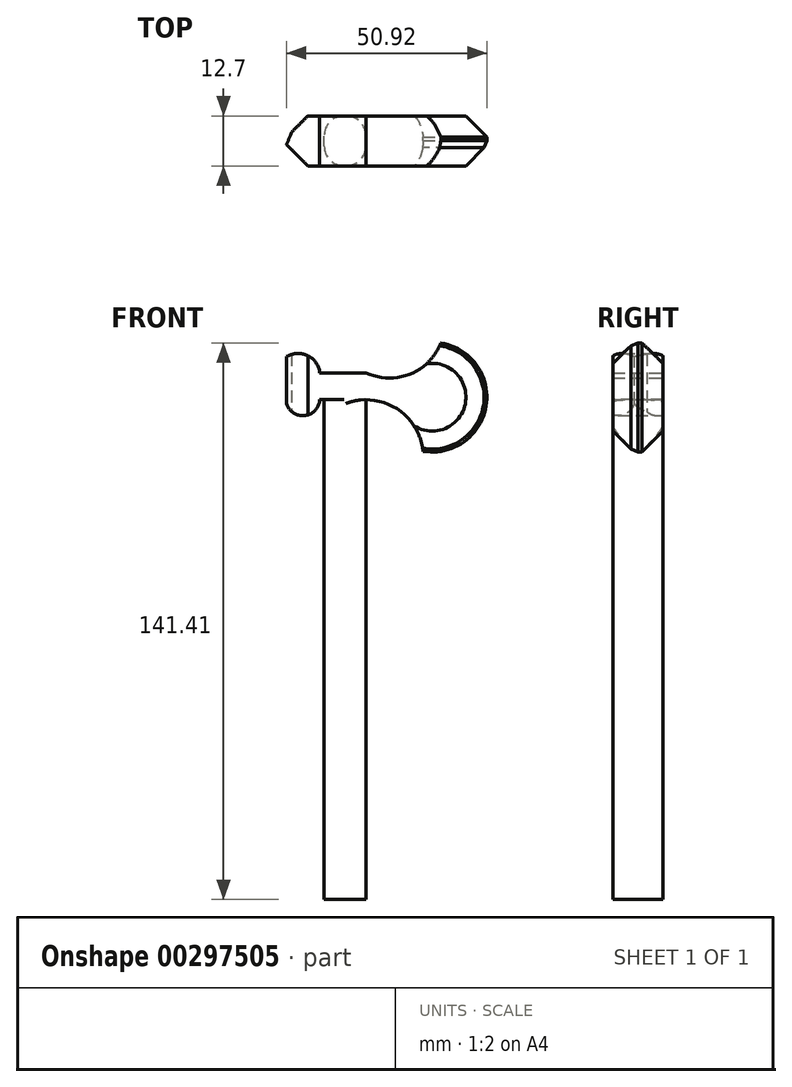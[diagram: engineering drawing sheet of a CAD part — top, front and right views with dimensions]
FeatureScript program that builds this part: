
annotation { "Feature Type Name" : "Feature", "Feature Type Description" : "" }
export const myFeature = defineFeature(function(context is Context, id is Id, definition is map)
    precondition{}
    {
        {
            var Q0;
            Q0=qCreatedBy(makeId("Front.planeOp"),FACE);
            var sketch = newSketch(context, id + "F0", { "sketchPlane" : qUnion([Q0])});
            skLineSegment(sketch, "E0", {"start": v(-22.66, 64.19) * mm, "end": v(-10.9, 64.19) * mm});
            skArc(sketch, "E1", {"start": v(3.57, 51.1) * mm, "mid": v(-1.15, 60.43) * mm, "end": v(-10.9, 64.19) * mm});
            skArc(sketch, "E2", {"start": v(3.57, 51.1) * mm, "mid": v(19.63, 62.58) * mm, "end": v(8.09, 78.6) * mm});
            skArc(sketch, "E3", {"start": v(-10.9, 71.03) * mm, "mid": v(0.23, 70.7) * mm, "end": v(8.09, 78.6) * mm});
            skLineSegment(sketch, "E4", {"start": v(-10.9, 71.03) * mm, "end": v(-22.66, 71.03) * mm});
            skArc(sketch, "E5", {"start": v(-22.66, 71.03) * mm, "mid": v(-25.84, 75.45) * mm, "end": v(-31.27, 75.02) * mm});
            skLineSegment(sketch, "E6", {"start": v(-31.27, 75.02) * mm, "end": v(-31.27, 63.99) * mm});
            skArc(sketch, "E7", {"start": v(-31.27, 63.99) * mm, "mid": v(-26.87, 60.15) * mm, "end": v(-22.66, 64.19) * mm});
            skLineSegment(sketch, "E8", {"start": v(-10.9, 64.19) * mm, "end": v(-10.9, -62.81) * mm});
            skLineSegment(sketch, "E9", {"start": v(-21.53, 64.19) * mm, "end": v(-21.53, -62.81) * mm});
            skLineSegment(sketch, "E10", {"start": v(-10.9, -62.81) * mm, "end": v(-21.53, -62.81) * mm});
            skSolve(sketch);
        }
        {
            var Q0;
            Q0 = qSketchRegion(id + "F0", true);
            extrude(context, id + "F1", {"entities" : qUnion([Q0]), "depth" : 6.35 * mm});
        }
        {
            var Q0;
            Q0 = qSketchRegion(id + "F0", true);
            extrude(context, id + "F2", {"entities" : qUnion([Q0]), "operationType" : NewBodyOperationType.ADD, "oppositeDirection" : true, "depth" : 6.35 * mm});
        }
        {
            var Q0;
            Q0=makeQuery(id+"F1.opExtrude","CAP_EDGE",EDGE,{"disambiguationData":[OSD([sQuery(id+"F0.wireOp",EDGE,"E2")])],"isStart":false});
            var Q1;
            Q1=makeQuery(id+"F2.opExtrude","CAP_EDGE",EDGE,{"disambiguationData":[OSD([sQuery(id+"F0.wireOp",EDGE,"E2")])],"isStart":false});
            chamfer(context, id + "F3", {"entities" : qUnion([Q0, Q1]), "width" : 5.33 * mm, "tangentPropagation" : true});
        }
        {
            var Q0;
            {var subQ0=sQuery(id+"F0.wireOp",EDGE,"E2");Q0=makeQuery(id+"F3.opChamfer","BLEND_EDGE",EDGE,{"blendedFrom":[makeQuery(id+"F1.opExtrude","CAP_EDGE",EDGE,{"disambiguationData":[OSD([subQ0])],"isStart":false}),makeQuery(id+"F2.boolean.opBoolean","MERGE",FACE,{"derivedFrom":[makeQuery(id+"F1.opExtrude","SWEPT_FACE",FACE,{"disambiguationData":[OSD([subQ0])]}),makeQuery(id+"F2.opExtrude","SWEPT_FACE",FACE,{"disambiguationData":[OSD([subQ0])]})]})],"blendedInto":[makeQuery(id+"F2.boolean.opBoolean","MERGE",FACE,{"derivedFrom":[makeQuery(id+"F1.opExtrude","SWEPT_FACE",FACE,{"disambiguationData":[OSD([subQ0])]}),makeQuery(id+"F2.opExtrude","SWEPT_FACE",FACE,{"disambiguationData":[OSD([subQ0])]})]})]});}
            chamfer(context, id + "F4", {"entities" : qUnion([Q0]), "width" : 2.54 * mm, "tangentPropagation" : true});
        }
        {
            var Q0;
            Q0=makeQuery(id+"F2.opExtrude","CAP_EDGE",EDGE,{"disambiguationData":[OSD([sQuery(id+"F0.wireOp",EDGE,"E6")])],"isStart":false});
            var Q1;
            Q1=makeQuery(id+"F1.opExtrude","CAP_EDGE",EDGE,{"disambiguationData":[OSD([sQuery(id+"F0.wireOp",EDGE,"E6")])],"isStart":false});
            chamfer(context, id + "F5", {"entities" : qUnion([Q0, Q1]), "width" : 5.6 * mm, "tangentPropagation" : true});
        }
        {
            var Q0;
            {var subQ0=sQuery(id+"F0.wireOp",EDGE,"E6");Q0=makeQuery(id+"F5.opChamfer","BLEND_EDGE",EDGE,{"blendedFrom":[makeQuery(id+"F2.opExtrude","CAP_EDGE",EDGE,{"disambiguationData":[OSD([subQ0])],"isStart":false}),makeQuery(id+"F2.boolean.opBoolean","MERGE",FACE,{"derivedFrom":[makeQuery(id+"F1.opExtrude","SWEPT_FACE",FACE,{"disambiguationData":[OSD([subQ0])]}),makeQuery(id+"F2.opExtrude","SWEPT_FACE",FACE,{"disambiguationData":[OSD([subQ0])]})]})],"blendedInto":[makeQuery(id+"F2.boolean.opBoolean","MERGE",FACE,{"derivedFrom":[makeQuery(id+"F1.opExtrude","SWEPT_FACE",FACE,{"disambiguationData":[OSD([subQ0])]}),makeQuery(id+"F2.opExtrude","SWEPT_FACE",FACE,{"disambiguationData":[OSD([subQ0])]})]})]});}
            chamfer(context, id + "F6", {"entities" : qUnion([Q0]), "width" : 5.08 * mm, "tangentPropagation" : true});
        }
        {
            var Q0;
            Q0=makeQuery(id+"F1.opExtrude","CAP_EDGE",EDGE,{"disambiguationData":[OSD([sQuery(id+"F0.wireOp",EDGE,"E8")])],"isStart":false});
            var Q1;
            Q1=makeQuery(id+"F2.opExtrude","CAP_EDGE",EDGE,{"disambiguationData":[OSD([sQuery(id+"F0.wireOp",EDGE,"E8")])],"isStart":false});
            var Q2;
            Q2=makeQuery(id+"F1.opExtrude","CAP_EDGE",EDGE,{"disambiguationData":[OSD([sQuery(id+"F0.wireOp",EDGE,"Ztdh6Nbt-9UEp-mU37-3oUx-bNuGYJWBlppO")])],"isStart":false});
            var Q3;
            Q3=makeQuery(id+"F2.opExtrude","CAP_EDGE",EDGE,{"disambiguationData":[OSD([sQuery(id+"F0.wireOp",EDGE,"Ztdh6Nbt-9UEp-mU37-3oUx-bNuGYJWBlppO")])],"isStart":false});
            fillet(context, id + "F7", {"entities" : qUnion([Q0, Q1, Q2, Q3]), "radius" : 5.08 * mm, "tangentPropagation" : true, "allowEdgeOverflow" : false});
        }
        {
            var Q0;
            Q0=makeQuery(id+"F2.opExtrude","CAP_EDGE",EDGE,{"disambiguationData":[OSD([sQuery(id+"F0.wireOp",EDGE,"E9")])],"isStart":false});
            var Q1;
            Q1=makeQuery(id+"F1.opExtrude","CAP_EDGE",EDGE,{"disambiguationData":[OSD([sQuery(id+"F0.wireOp",EDGE,"E9")])],"isStart":false});
            fillet(context, id + "F8", {"entities" : qUnion([Q0, Q1]), "radius" : 5.08 * mm, "tangentPropagation" : true, "allowEdgeOverflow" : false});
        }
    });
